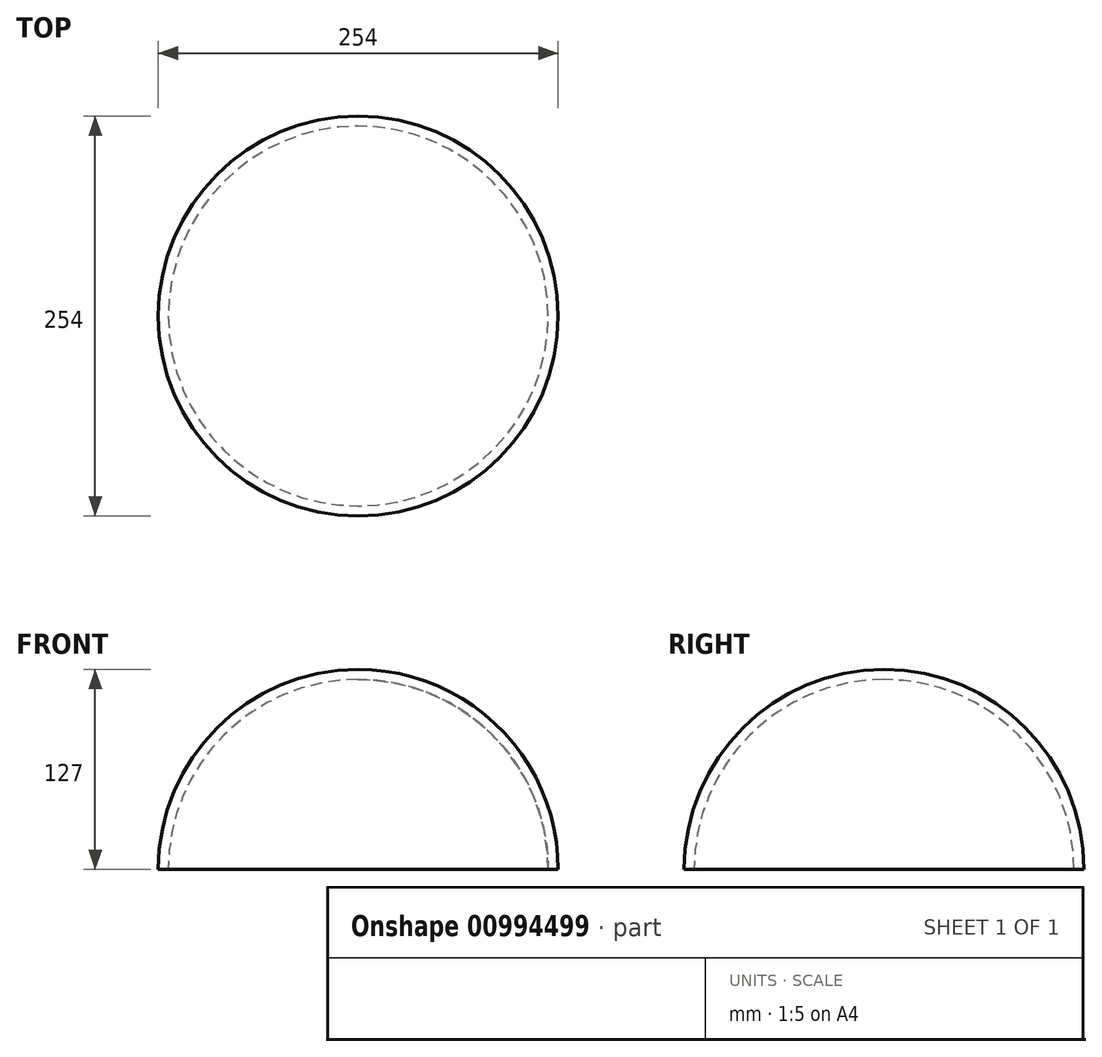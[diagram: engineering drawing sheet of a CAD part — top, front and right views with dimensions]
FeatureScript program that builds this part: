
annotation { "Feature Type Name" : "Feature", "Feature Type Description" : "" }
export const myFeature = defineFeature(function(context is Context, id is Id, definition is map)
    precondition{}
    {
        {
            var Q0;
            Q0=qCreatedBy(makeId("Front.planeOp"),FACE);
            var sketch = newSketch(context, id + "F0", { "sketchPlane" : qUnion([Q0])});
            skArc(sketch, "E0", {"start": v(120.65, 0) * mm, "mid": v(85.31, 85.31) * mm, "end": v(0, 120.65) * mm});
            skArc(sketch, "E1.0", {"start": v(127, 0) * mm, "mid": v(89.8, 89.8) * mm, "end": v(0, 127) * mm});
            skLineSegment(sketch, "E2", {"start": v(0, 127) * mm, "end": v(0, 120.65) * mm});
            skLineSegment(sketch, "E3", {"start": v(127, 0) * mm, "end": v(120.65, 0) * mm});
            skLineSegment(sketch, "E4", {"start": v(0, 0) * mm, "end": v(0, 205.38) * mm});
            skLineSegment(sketch, "E5", {"start": v(0, 205.38) * mm, "end": v(0, 162.61) * mm});
            skSolve(sketch);
        }
        {
            var Q0;
            {var subQ0=sQuery(id+"F0.wireOp",EDGE,"E0");Q0=makeQuery(id+"F0.imprint","IMPRINT",FACE,{"disambiguationData":[TD([[makeQuery(id+"F0.imprint","IMPRINT",EDGE,{"derivedFrom":subQ0}),-1.0]])]});}
            var Q1;
            Q1=sQuery(id+"F0.wireOp",EDGE,"E4");
            revolve(context, id + "F1", {"surfaceOperationType" : NewSurfaceOperationType.NEW, "entities" : qUnion([Q0]), "axis" : qUnion([Q1]), "revolveType" : RevolveType.FULL});
        }
    });
